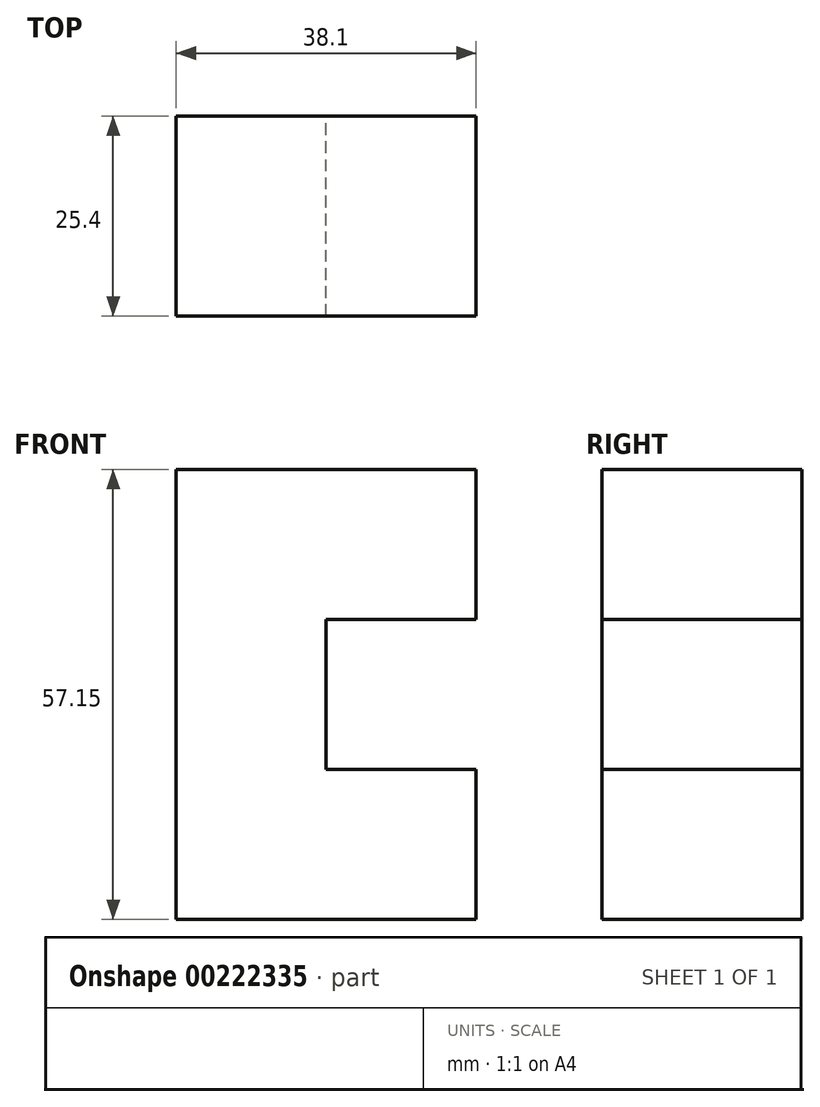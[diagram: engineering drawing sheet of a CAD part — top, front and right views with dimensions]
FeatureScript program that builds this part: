
annotation { "Feature Type Name" : "Feature", "Feature Type Description" : "" }
export const myFeature = defineFeature(function(context is Context, id is Id, definition is map)
    precondition{}
    {
        {
            var Q0;
            Q0=qCreatedBy(makeId("Front.planeOp"),FACE);
            var sketch = newSketch(context, id + "F0", { "sketchPlane" : qUnion([Q0])});
            skLineSegment(sketch, "E0.bottom", {"start": v(-43.35, 10.96) * mm, "end": v(-62.4, 10.96) * mm});
            skLineSegment(sketch, "E0.top", {"start": v(-43.35, 68.11) * mm, "end": v(-62.4, 68.11) * mm});
            skLineSegment(sketch, "E0.left", {"start": v(-43.35, 10.96) * mm, "end": v(-43.35, 68.11) * mm});
            skLineSegment(sketch, "E0.right", {"start": v(-62.4, 10.96) * mm, "end": v(-62.4, 68.11) * mm});
            skPoint(sketch, "E0.middle", {"position": v(-52.87, 39.54) * mm});
            skLineSegment(sketch, "E1.bottom", {"start": v(-24.3, 49.06) * mm, "end": v(-43.35, 49.06) * mm});
            skLineSegment(sketch, "E1.top", {"start": v(-24.3, 68.11) * mm, "end": v(-43.35, 68.11) * mm});
            skLineSegment(sketch, "E1.left", {"start": v(-24.3, 49.06) * mm, "end": v(-24.3, 68.11) * mm});
            skLineSegment(sketch, "E1.right", {"start": v(-43.35, 49.06) * mm, "end": v(-43.35, 68.11) * mm});
            skPoint(sketch, "E1.middle", {"position": v(-33.82, 58.59) * mm});
            skLineSegment(sketch, "E2.bottom", {"start": v(-24.3, 10.96) * mm, "end": v(-43.35, 10.96) * mm});
            skLineSegment(sketch, "E2.top", {"start": v(-24.3, 30.01) * mm, "end": v(-43.35, 30.01) * mm});
            skLineSegment(sketch, "E2.left", {"start": v(-24.3, 10.96) * mm, "end": v(-24.3, 30.01) * mm});
            skLineSegment(sketch, "E2.right", {"start": v(-43.35, 10.96) * mm, "end": v(-43.35, 30.01) * mm});
            skPoint(sketch, "E2.middle", {"position": v(-33.82, 20.49) * mm});
            skSolve(sketch);
        }
        {
            var Q0;
            Q0 = qSketchRegion(id + "F0", true);
            extrude(context, id + "F1", {"entities" : qUnion([Q0]), "endBound" : BoundingType.SYMMETRIC, "depth" : 25.4 * mm});
        }
        {
            var Q0;
            Q0 = qSketchRegion(id + "F0", true);
            extrude(context, id + "F2", {"entities" : qUnion([Q0]), "operationType" : NewBodyOperationType.ADD, "endBound" : BoundingType.SYMMETRIC, "depth" : 25.4 * mm});
        }
    });
